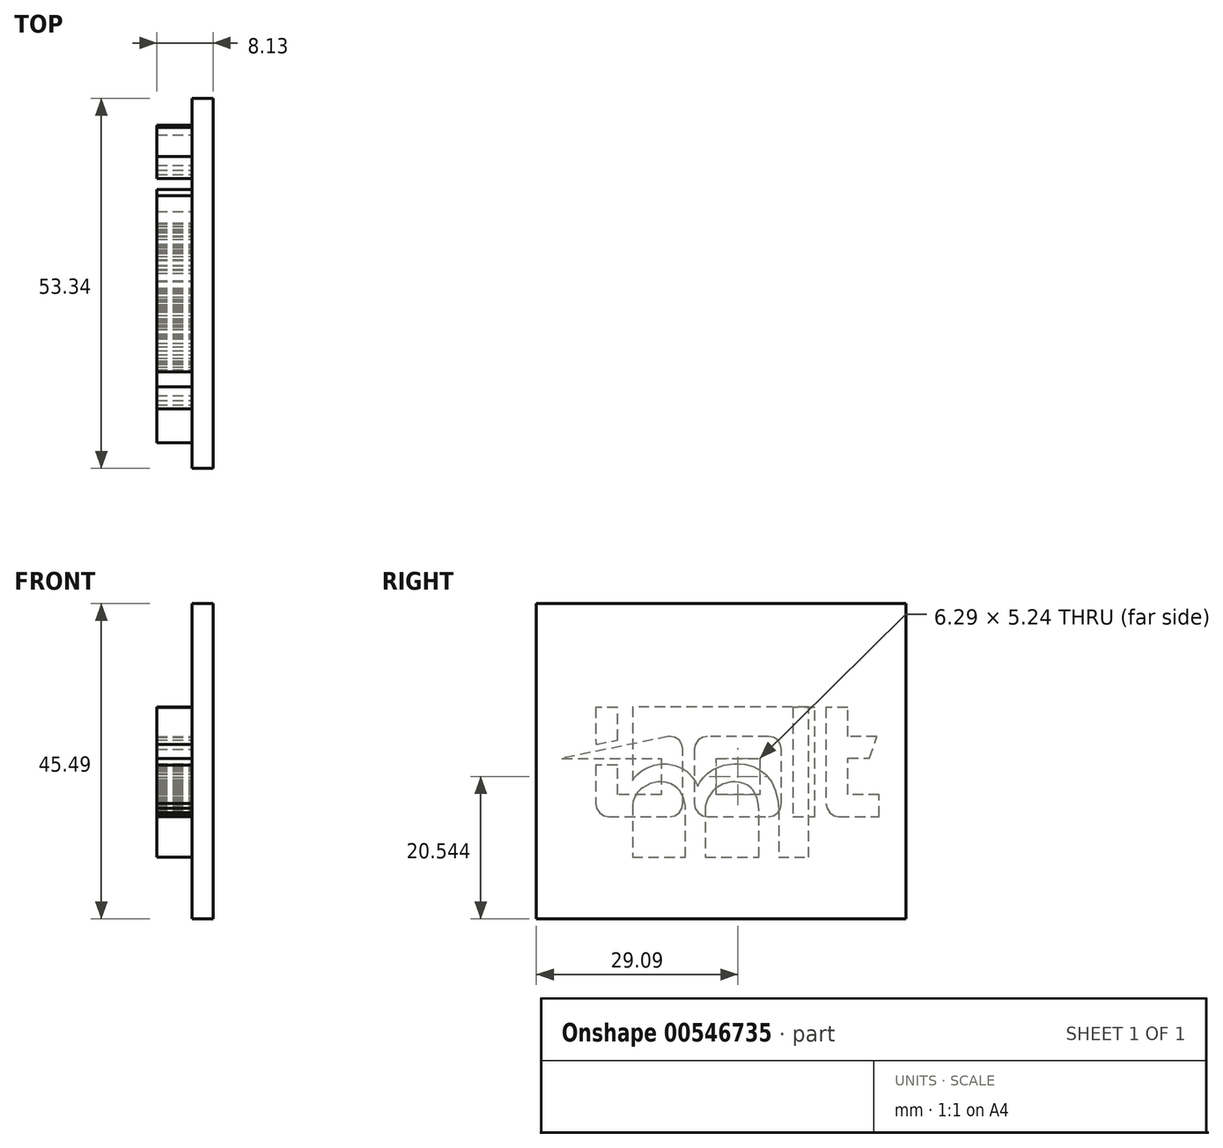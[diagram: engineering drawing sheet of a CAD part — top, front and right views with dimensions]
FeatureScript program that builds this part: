
annotation { "Feature Type Name" : "Feature", "Feature Type Description" : "" }
export const myFeature = defineFeature(function(context is Context, id is Id, definition is map)
    precondition{}
    {
        {
            var Q0;
            Q0=qCreatedBy(makeId("Right.planeOp"),FACE);
            var sketch = newSketch(context, id + "F0", { "sketchPlane" : qUnion([Q0])});
            skLineSegment(sketch, "E0", {"start": v(-5.03, -6.77) * mm, "end": v(-5.03, -6.38) * mm});
            skLineSegment(sketch, "E1", {"start": v(-5.03, -6.38) * mm, "end": v(-5.3, -5.2) * mm});
            skLineSegment(sketch, "E2", {"start": v(-5.3, -5.2) * mm, "end": v(-5.9, -4.14) * mm});
            skLineSegment(sketch, "E3", {"start": v(-5.9, -4.14) * mm, "end": v(-6.07, -3.97) * mm});
            skLineSegment(sketch, "E4", {"start": v(-6.07, -3.97) * mm, "end": v(-6.19, -3.84) * mm});
            skLineSegment(sketch, "E5", {"start": v(-6.19, -3.84) * mm, "end": v(-6.6, -3.5) * mm});
            skLineSegment(sketch, "E6", {"start": v(-6.6, -3.5) * mm, "end": v(-7.23, -3.15) * mm});
            skLineSegment(sketch, "E7", {"start": v(-7.23, -3.15) * mm, "end": v(-7.93, -2.93) * mm});
            skLineSegment(sketch, "E8", {"start": v(-7.93, -2.93) * mm, "end": v(-8.51, -2.86) * mm});
            skLineSegment(sketch, "E9", {"start": v(-8.51, -2.86) * mm, "end": v(-8.7, -2.86) * mm});
            skLineSegment(sketch, "E10", {"start": v(-8.7, -2.86) * mm, "end": v(-9.07, -2.86) * mm});
            skLineSegment(sketch, "E11", {"start": v(-9.07, -2.86) * mm, "end": v(-10.16, -3.13) * mm});
            skLineSegment(sketch, "E12", {"start": v(-10.16, -3.13) * mm, "end": v(-11.26, -3.73) * mm});
            skLineSegment(sketch, "E13", {"start": v(-11.26, -3.73) * mm, "end": v(-11.44, -3.89) * mm});
            skLineSegment(sketch, "E14", {"start": v(-11.44, -3.89) * mm, "end": v(-11.58, -4) * mm});
            skLineSegment(sketch, "E15", {"start": v(-11.58, -4) * mm, "end": v(-11.96, -4.4) * mm});
            skLineSegment(sketch, "E16", {"start": v(-11.96, -4.4) * mm, "end": v(-12.35, -5) * mm});
            skLineSegment(sketch, "E17", {"start": v(-12.35, -5) * mm, "end": v(-12.6, -5.67) * mm});
            skLineSegment(sketch, "E18", {"start": v(-12.6, -5.67) * mm, "end": v(-12.7, -6.2) * mm});
            skLineSegment(sketch, "E19", {"start": v(-12.7, -6.2) * mm, "end": v(-12.7, -6.38) * mm});
            skLineSegment(sketch, "E20", {"start": v(-12.7, -6.38) * mm, "end": v(-12.7, -13.74) * mm});
            skLineSegment(sketch, "E21", {"start": v(-12.7, -13.74) * mm, "end": v(-5.03, -13.74) * mm});
            skLineSegment(sketch, "E22", {"start": v(-5.03, -13.74) * mm, "end": v(-5.03, -6.77) * mm});
            skLineSegment(sketch, "E23", {"start": v(-12.7, 7.94) * mm, "end": v(-12.7, -2.7) * mm});
            skLineSegment(sketch, "E24", {"start": v(-12.7, -2.7) * mm, "end": v(-12.64, -2.58) * mm});
            skLineSegment(sketch, "E25", {"start": v(-12.64, -2.58) * mm, "end": v(-12.4, -2.23) * mm});
            skLineSegment(sketch, "E26", {"start": v(-12.4, -2.23) * mm, "end": v(-12, -1.78) * mm});
            skLineSegment(sketch, "E27", {"start": v(-12, -1.78) * mm, "end": v(-11.5, -1.36) * mm});
            skLineSegment(sketch, "E28", {"start": v(-11.5, -1.36) * mm, "end": v(-11.06, -1.08) * mm});
            skLineSegment(sketch, "E29", {"start": v(-11.06, -1.08) * mm, "end": v(-10.91, -1) * mm});
            skLineSegment(sketch, "E30", {"start": v(-10.91, -1) * mm, "end": v(-10.71, -0.88) * mm});
            skLineSegment(sketch, "E31", {"start": v(-10.71, -0.88) * mm, "end": v(-9.6, -0.45) * mm});
            skLineSegment(sketch, "E32", {"start": v(-9.6, -0.45) * mm, "end": v(-8.51, -0.24) * mm});
            skLineSegment(sketch, "E33", {"start": v(-8.51, -0.24) * mm, "end": v(-8.15, -0.24) * mm});
            skLineSegment(sketch, "E34", {"start": v(-8.15, -0.24) * mm, "end": v(-7.74, -0.24) * mm});
            skLineSegment(sketch, "E35", {"start": v(-7.74, -0.24) * mm, "end": v(-6.5, -0.5) * mm});
            skLineSegment(sketch, "E36", {"start": v(-6.5, -0.5) * mm, "end": v(-5.32, -1.04) * mm});
            skLineSegment(sketch, "E37", {"start": v(-5.32, -1.04) * mm, "end": v(-5.11, -1.19) * mm});
            skLineSegment(sketch, "E38", {"start": v(-5.11, -1.19) * mm, "end": v(-4.96, -1.3) * mm});
            skLineSegment(sketch, "E39", {"start": v(-4.96, -1.3) * mm, "end": v(-4.52, -1.67) * mm});
            skLineSegment(sketch, "E40", {"start": v(-4.52, -1.67) * mm, "end": v(-4.02, -2.23) * mm});
            skLineSegment(sketch, "E41", {"start": v(-4.02, -2.23) * mm, "end": v(-3.6, -2.85) * mm});
            skLineSegment(sketch, "E42", {"start": v(-3.6, -2.85) * mm, "end": v(-3.35, -3.35) * mm});
            skLineSegment(sketch, "E43", {"start": v(-3.35, -3.35) * mm, "end": v(-3.29, -3.53) * mm});
            skLineSegment(sketch, "E44", {"start": v(-3.29, -3.53) * mm, "end": v(-3.22, -3.35) * mm});
            skLineSegment(sketch, "E45", {"start": v(-3.22, -3.35) * mm, "end": v(-2.95, -2.84) * mm});
            skLineSegment(sketch, "E46", {"start": v(-2.95, -2.84) * mm, "end": v(-2.47, -2.2) * mm});
            skLineSegment(sketch, "E47", {"start": v(-2.47, -2.2) * mm, "end": v(-1.87, -1.64) * mm});
            skLineSegment(sketch, "E48", {"start": v(-1.87, -1.64) * mm, "end": v(-1.35, -1.27) * mm});
            skLineSegment(sketch, "E49", {"start": v(-1.35, -1.27) * mm, "end": v(-1.17, -1.16) * mm});
            skLineSegment(sketch, "E50", {"start": v(-1.17, -1.16) * mm, "end": v(-0.92, -1.01) * mm});
            skLineSegment(sketch, "E51", {"start": v(-0.92, -1.01) * mm, "end": v(0.47, -0.47) * mm});
            skLineSegment(sketch, "E52", {"start": v(0.47, -0.47) * mm, "end": v(1.98, -0.24) * mm});
            skLineSegment(sketch, "E53", {"start": v(1.98, -0.24) * mm, "end": v(2.29, -0.24) * mm});
            skLineSegment(sketch, "E54", {"start": v(2.29, -0.24) * mm, "end": v(2.6, -0.25) * mm});
            skLineSegment(sketch, "E55", {"start": v(2.6, -0.25) * mm, "end": v(3.55, -0.36) * mm});
            skLineSegment(sketch, "E56", {"start": v(3.55, -0.36) * mm, "end": v(4.71, -0.67) * mm});
            skLineSegment(sketch, "E57", {"start": v(4.71, -0.67) * mm, "end": v(5.75, -1.19) * mm});
            skLineSegment(sketch, "E58", {"start": v(5.75, -1.19) * mm, "end": v(6.44, -1.72) * mm});
            skLineSegment(sketch, "E59", {"start": v(6.44, -1.72) * mm, "end": v(6.64, -1.93) * mm});
            skLineSegment(sketch, "E60", {"start": v(6.64, -1.93) * mm, "end": v(6.85, -2.14) * mm});
            skLineSegment(sketch, "E61", {"start": v(6.85, -2.14) * mm, "end": v(7.37, -2.9) * mm});
            skLineSegment(sketch, "E62", {"start": v(7.37, -2.9) * mm, "end": v(7.92, -4.1) * mm});
            skLineSegment(sketch, "E63", {"start": v(7.92, -4.1) * mm, "end": v(8.26, -5.56) * mm});
            skLineSegment(sketch, "E64", {"start": v(8.26, -5.56) * mm, "end": v(8.38, -6.85) * mm});
            skLineSegment(sketch, "E65", {"start": v(8.38, -6.85) * mm, "end": v(8.38, -7.28) * mm});
            skLineSegment(sketch, "E66", {"start": v(8.38, -7.28) * mm, "end": v(8.38, -13.74) * mm});
            skLineSegment(sketch, "E67", {"start": v(8.38, -13.74) * mm, "end": v(12.7, -13.74) * mm});
            skLineSegment(sketch, "E68", {"start": v(12.7, -13.74) * mm, "end": v(12.7, 7.94) * mm});
            skLineSegment(sketch, "E69", {"start": v(12.7, 7.94) * mm, "end": v(-12.7, 7.94) * mm});
            skLineSegment(sketch, "E70", {"start": v(1.93, -2.86) * mm, "end": v(1.54, -2.86) * mm});
            skLineSegment(sketch, "E71", {"start": v(1.54, -2.86) * mm, "end": v(0.37, -3.17) * mm});
            skLineSegment(sketch, "E72", {"start": v(0.37, -3.17) * mm, "end": v(-0.75, -3.83) * mm});
            skLineSegment(sketch, "E73", {"start": v(-0.75, -3.83) * mm, "end": v(-0.94, -4) * mm});
            skLineSegment(sketch, "E74", {"start": v(-0.94, -4) * mm, "end": v(-1.13, -4.18) * mm});
            skLineSegment(sketch, "E75", {"start": v(-1.13, -4.18) * mm, "end": v(-1.84, -5.24) * mm});
            skLineSegment(sketch, "E76", {"start": v(-1.84, -5.24) * mm, "end": v(-2.18, -6.36) * mm});
            skLineSegment(sketch, "E77", {"start": v(-2.18, -6.36) * mm, "end": v(-2.18, -6.73) * mm});
            skLineSegment(sketch, "E78", {"start": v(-2.18, -6.73) * mm, "end": v(-2.18, -13.74) * mm});
            skLineSegment(sketch, "E79", {"start": v(-2.18, -13.74) * mm, "end": v(5.53, -13.74) * mm});
            skLineSegment(sketch, "E80", {"start": v(5.53, -13.74) * mm, "end": v(5.53, -7.36) * mm});
            skLineSegment(sketch, "E81", {"start": v(5.53, -7.36) * mm, "end": v(5.53, -7.08) * mm});
            skLineSegment(sketch, "E82", {"start": v(5.53, -7.08) * mm, "end": v(5.46, -6.22) * mm});
            skLineSegment(sketch, "E83", {"start": v(5.46, -6.22) * mm, "end": v(5.27, -5.26) * mm});
            skLineSegment(sketch, "E84", {"start": v(5.27, -5.26) * mm, "end": v(4.95, -4.48) * mm});
            skLineSegment(sketch, "E85", {"start": v(4.95, -4.48) * mm, "end": v(4.64, -4) * mm});
            skLineSegment(sketch, "E86", {"start": v(4.64, -4) * mm, "end": v(4.52, -3.86) * mm});
            skLineSegment(sketch, "E87", {"start": v(4.52, -3.86) * mm, "end": v(4.4, -3.73) * mm});
            skLineSegment(sketch, "E88", {"start": v(4.4, -3.73) * mm, "end": v(4, -3.4) * mm});
            skLineSegment(sketch, "E89", {"start": v(4, -3.4) * mm, "end": v(3.38, -3.1) * mm});
            skLineSegment(sketch, "E90", {"start": v(3.38, -3.1) * mm, "end": v(2.69, -2.91) * mm});
            skLineSegment(sketch, "E91", {"start": v(2.69, -2.91) * mm, "end": v(2.12, -2.86) * mm});
            skLineSegment(sketch, "E92", {"start": v(2.12, -2.86) * mm, "end": v(1.93, -2.86) * mm});
            skSolve(sketch);
        }
        {
            var Q0;
            Q0=makeQuery(id+"F0.imprint","IMPRINT",FACE,{"disambiguationData":[TD([[makeQuery(id+"F0.imprint","IMPRINT",EDGE,{"derivedFrom":sQuery(id+"F0.wireOp",EDGE,"E23")}),1.0]])]});
            var Q1;
            Q1=makeQuery(id+"F0.imprint","IMPRINT",FACE,{"disambiguationData":[TD([[makeQuery(id+"F0.imprint","IMPRINT",EDGE,{"derivedFrom":sQuery(id+"F0.wireOp",EDGE,"E0")}),1.0]])]});
            var Q2;
            Q2=makeQuery(id+"F0.imprint","IMPRINT",FACE,{"disambiguationData":[TD([[makeQuery(id+"F0.imprint","IMPRINT",EDGE,{"derivedFrom":sQuery(id+"F0.wireOp",EDGE,"E70")}),1.0]])]});
            extrude(context, id + "F1", {"entities" : qUnion([Q0, Q1, Q2]), "depth" : -5.08 * mm, "offsetDistance" : 25.4 * mm});
        }
        {
            var Q0;
            Q0=qCreatedBy(makeId("Right.planeOp"),FACE);
            var sketch = newSketch(context, id + "F2", { "sketchPlane" : qUnion([Q0])});
            skLineSegment(sketch, "E93.bottom", {"start": v(-26.57, 22.85) * mm, "end": v(26.77, 22.85) * mm});
            skLineSegment(sketch, "E93.top", {"start": v(-26.57, -22.64) * mm, "end": v(26.77, -22.64) * mm});
            skLineSegment(sketch, "E93.left", {"start": v(-26.57, 22.85) * mm, "end": v(-26.57, -22.64) * mm});
            skLineSegment(sketch, "E93.right", {"start": v(26.77, 22.85) * mm, "end": v(26.77, -22.64) * mm});
            skSolve(sketch);
        }
        {
            var Q0;
            Q0 = qSketchRegion(id + "F2", true);
            extrude(context, id + "F3", {"entities" : qUnion([Q0]), "depth" : 3.05 * mm, "offsetDistance" : 25.4 * mm});
        }
        {
            var Q0;
            Q0=qCreatedBy(makeId("Right.planeOp"),FACE);
            var sketch = newSketch(context, id + "F4", { "sketchPlane" : qUnion([Q0])});
            skLineSegment(sketch, "E94", {"start": v(18.38, -4.72) * mm, "end": v(18.38, 0.53) * mm});
            skLineSegment(sketch, "E95", {"start": v(18.38, 0.53) * mm, "end": v(21.51, 0.53) * mm});
            skLineSegment(sketch, "E96", {"start": v(21.51, 0.53) * mm, "end": v(22.56, 3.67) * mm});
            skLineSegment(sketch, "E97", {"start": v(22.56, 3.67) * mm, "end": v(18.38, 3.67) * mm});
            skLineSegment(sketch, "E98", {"start": v(18.38, 3.67) * mm, "end": v(18.38, 7.85) * mm});
            skLineSegment(sketch, "E99", {"start": v(18.38, 7.85) * mm, "end": v(15.23, 7.85) * mm});
            skLineSegment(sketch, "E100", {"start": v(15.23, 7.85) * mm, "end": v(15.23, -5.76) * mm});
            skLineSegment(sketch, "E101", {"start": v(15.23, -5.76) * mm, "end": v(15.23, -6) * mm});
            skLineSegment(sketch, "E102", {"start": v(15.23, -6) * mm, "end": v(15.36, -6.68) * mm});
            skLineSegment(sketch, "E103", {"start": v(15.36, -6.68) * mm, "end": v(15.76, -7.33) * mm});
            skLineSegment(sketch, "E104", {"start": v(15.76, -7.33) * mm, "end": v(16.41, -7.73) * mm});
            skLineSegment(sketch, "E105", {"start": v(16.41, -7.73) * mm, "end": v(17.1, -7.86) * mm});
            skLineSegment(sketch, "E106", {"start": v(17.1, -7.86) * mm, "end": v(17.33, -7.86) * mm});
            skLineSegment(sketch, "E107", {"start": v(17.33, -7.86) * mm, "end": v(22.87, -7.86) * mm});
            skLineSegment(sketch, "E108", {"start": v(22.87, -7.86) * mm, "end": v(22.87, -4.72) * mm});
            skLineSegment(sketch, "E109", {"start": v(22.87, -4.72) * mm, "end": v(18.38, -4.72) * mm});
            skLineSegment(sketch, "E110", {"start": v(10.45, -7.86) * mm, "end": v(13.6, -7.86) * mm});
            skLineSegment(sketch, "E111", {"start": v(13.6, -7.86) * mm, "end": v(13.6, 7.86) * mm});
            skLineSegment(sketch, "E112", {"start": v(13.6, 7.86) * mm, "end": v(10.45, 7.86) * mm});
            skLineSegment(sketch, "E113", {"start": v(10.45, 7.86) * mm, "end": v(10.45, -7.86) * mm});
            skLineSegment(sketch, "E114", {"start": v(5.66, -4.72) * mm, "end": v(-0.62, -4.72) * mm});
            skLineSegment(sketch, "E115", {"start": v(-0.62, -4.72) * mm, "end": v(-0.62, 0.52) * mm});
            skLineSegment(sketch, "E116", {"start": v(-0.62, 0.52) * mm, "end": v(5.66, 0.52) * mm});
            skLineSegment(sketch, "E117", {"start": v(5.66, 0.52) * mm, "end": v(5.66, -4.72) * mm});
            skLineSegment(sketch, "E118", {"start": v(6.71, 3.67) * mm, "end": v(-1.67, 3.67) * mm});
            skLineSegment(sketch, "E119", {"start": v(-1.67, 3.67) * mm, "end": v(-1.9, 3.67) * mm});
            skLineSegment(sketch, "E120", {"start": v(-1.9, 3.67) * mm, "end": v(-2.59, 3.54) * mm});
            skLineSegment(sketch, "E121", {"start": v(-2.59, 3.54) * mm, "end": v(-3.24, 3.14) * mm});
            skLineSegment(sketch, "E122", {"start": v(-3.24, 3.14) * mm, "end": v(-3.64, 2.49) * mm});
            skLineSegment(sketch, "E123", {"start": v(-3.64, 2.49) * mm, "end": v(-3.77, 1.8) * mm});
            skLineSegment(sketch, "E124", {"start": v(-3.77, 1.8) * mm, "end": v(-3.77, 1.57) * mm});
            skLineSegment(sketch, "E125", {"start": v(-3.77, 1.57) * mm, "end": v(-3.77, -5.76) * mm});
            skLineSegment(sketch, "E126", {"start": v(-3.77, -5.76) * mm, "end": v(-3.77, -6) * mm});
            skLineSegment(sketch, "E127", {"start": v(-3.77, -6) * mm, "end": v(-3.64, -6.68) * mm});
            skLineSegment(sketch, "E128", {"start": v(-3.64, -6.68) * mm, "end": v(-3.24, -7.33) * mm});
            skLineSegment(sketch, "E129", {"start": v(-3.24, -7.33) * mm, "end": v(-2.59, -7.73) * mm});
            skLineSegment(sketch, "E130", {"start": v(-2.59, -7.73) * mm, "end": v(-1.9, -7.86) * mm});
            skLineSegment(sketch, "E131", {"start": v(-1.9, -7.86) * mm, "end": v(-1.67, -7.86) * mm});
            skLineSegment(sketch, "E132", {"start": v(-1.67, -7.86) * mm, "end": v(6.71, -7.86) * mm});
            skLineSegment(sketch, "E133", {"start": v(6.71, -7.86) * mm, "end": v(6.94, -7.86) * mm});
            skLineSegment(sketch, "E134", {"start": v(6.94, -7.86) * mm, "end": v(7.63, -7.73) * mm});
            skLineSegment(sketch, "E135", {"start": v(7.63, -7.73) * mm, "end": v(8.28, -7.33) * mm});
            skLineSegment(sketch, "E136", {"start": v(8.28, -7.33) * mm, "end": v(8.67, -6.68) * mm});
            skLineSegment(sketch, "E137", {"start": v(8.67, -6.68) * mm, "end": v(8.8, -6) * mm});
            skLineSegment(sketch, "E138", {"start": v(8.8, -6) * mm, "end": v(8.8, -5.76) * mm});
            skLineSegment(sketch, "E139", {"start": v(8.8, -5.76) * mm, "end": v(8.8, 1.57) * mm});
            skLineSegment(sketch, "E140", {"start": v(8.8, 1.57) * mm, "end": v(8.8, 1.8) * mm});
            skLineSegment(sketch, "E141", {"start": v(8.8, 1.8) * mm, "end": v(8.67, 2.49) * mm});
            skLineSegment(sketch, "E142", {"start": v(8.67, 2.49) * mm, "end": v(8.28, 3.14) * mm});
            skLineSegment(sketch, "E143", {"start": v(8.28, 3.14) * mm, "end": v(7.63, 3.54) * mm});
            skLineSegment(sketch, "E144", {"start": v(7.63, 3.54) * mm, "end": v(6.94, 3.67) * mm});
            skLineSegment(sketch, "E145", {"start": v(6.94, 3.67) * mm, "end": v(6.71, 3.67) * mm});
            skLineSegment(sketch, "E146", {"start": v(-14.84, 3.17) * mm, "end": v(-14.84, 7.86) * mm});
            skLineSegment(sketch, "E147", {"start": v(-14.84, 7.86) * mm, "end": v(-17.98, 7.86) * mm});
            skLineSegment(sketch, "E148", {"start": v(-17.98, 7.86) * mm, "end": v(-17.97, 2.52) * mm});
            skLineSegment(sketch, "E149", {"start": v(-17.97, 2.52) * mm, "end": v(-14.84, 3.17) * mm});
            skLineSegment(sketch, "E150", {"start": v(-7.5, 3.67) * mm, "end": v(-22.87, 0.52) * mm});
            skLineSegment(sketch, "E151", {"start": v(-22.87, 0.52) * mm, "end": v(-8.55, 0.52) * mm});
            skLineSegment(sketch, "E152", {"start": v(-8.55, 0.52) * mm, "end": v(-8.55, -4.72) * mm});
            skLineSegment(sketch, "E153", {"start": v(-8.55, -4.72) * mm, "end": v(-14.84, -4.72) * mm});
            skLineSegment(sketch, "E154", {"start": v(-14.84, -4.72) * mm, "end": v(-14.84, -0.47) * mm});
            skLineSegment(sketch, "E155", {"start": v(-14.84, -0.47) * mm, "end": v(-17.98, -0.47) * mm});
            skLineSegment(sketch, "E156", {"start": v(-17.98, -0.47) * mm, "end": v(-17.98, -5.76) * mm});
            skLineSegment(sketch, "E157", {"start": v(-17.98, -5.76) * mm, "end": v(-17.98, -6) * mm});
            skLineSegment(sketch, "E158", {"start": v(-17.98, -6) * mm, "end": v(-17.85, -6.68) * mm});
            skLineSegment(sketch, "E159", {"start": v(-17.85, -6.68) * mm, "end": v(-17.46, -7.33) * mm});
            skLineSegment(sketch, "E160", {"start": v(-17.46, -7.33) * mm, "end": v(-16.8, -7.73) * mm});
            skLineSegment(sketch, "E161", {"start": v(-16.8, -7.73) * mm, "end": v(-16.11, -7.86) * mm});
            skLineSegment(sketch, "E162", {"start": v(-16.11, -7.86) * mm, "end": v(-15.89, -7.86) * mm});
            skLineSegment(sketch, "E163", {"start": v(-15.89, -7.86) * mm, "end": v(-7.5, -7.86) * mm});
            skLineSegment(sketch, "E164", {"start": v(-7.5, -7.86) * mm, "end": v(-7.27, -7.86) * mm});
            skLineSegment(sketch, "E165", {"start": v(-7.27, -7.86) * mm, "end": v(-6.59, -7.73) * mm});
            skLineSegment(sketch, "E166", {"start": v(-6.59, -7.73) * mm, "end": v(-5.93, -7.33) * mm});
            skLineSegment(sketch, "E167", {"start": v(-5.93, -7.33) * mm, "end": v(-5.54, -6.68) * mm});
            skLineSegment(sketch, "E168", {"start": v(-5.54, -6.68) * mm, "end": v(-5.4, -6) * mm});
            skLineSegment(sketch, "E169", {"start": v(-5.4, -6) * mm, "end": v(-5.4, -5.76) * mm});
            skLineSegment(sketch, "E170", {"start": v(-5.4, -5.76) * mm, "end": v(-5.4, 1.57) * mm});
            skLineSegment(sketch, "E171", {"start": v(-5.4, 1.57) * mm, "end": v(-5.4, 1.8) * mm});
            skLineSegment(sketch, "E172", {"start": v(-5.4, 1.8) * mm, "end": v(-5.54, 2.49) * mm});
            skLineSegment(sketch, "E173", {"start": v(-5.54, 2.49) * mm, "end": v(-5.93, 3.14) * mm});
            skLineSegment(sketch, "E174", {"start": v(-5.93, 3.14) * mm, "end": v(-6.59, 3.54) * mm});
            skLineSegment(sketch, "E175", {"start": v(-6.59, 3.54) * mm, "end": v(-7.27, 3.67) * mm});
            skLineSegment(sketch, "E176", {"start": v(-7.27, 3.67) * mm, "end": v(-7.5, 3.67) * mm});
            skSolve(sketch);
        }
        {
            var Q0;
            Q0 = qSketchRegion(id + "F4", true);
            extrude(context, id + "F5", {"entities" : qUnion([Q0]), "depth" : -5.08 * mm, "offsetDistance" : 25.4 * mm});
        }
    });
